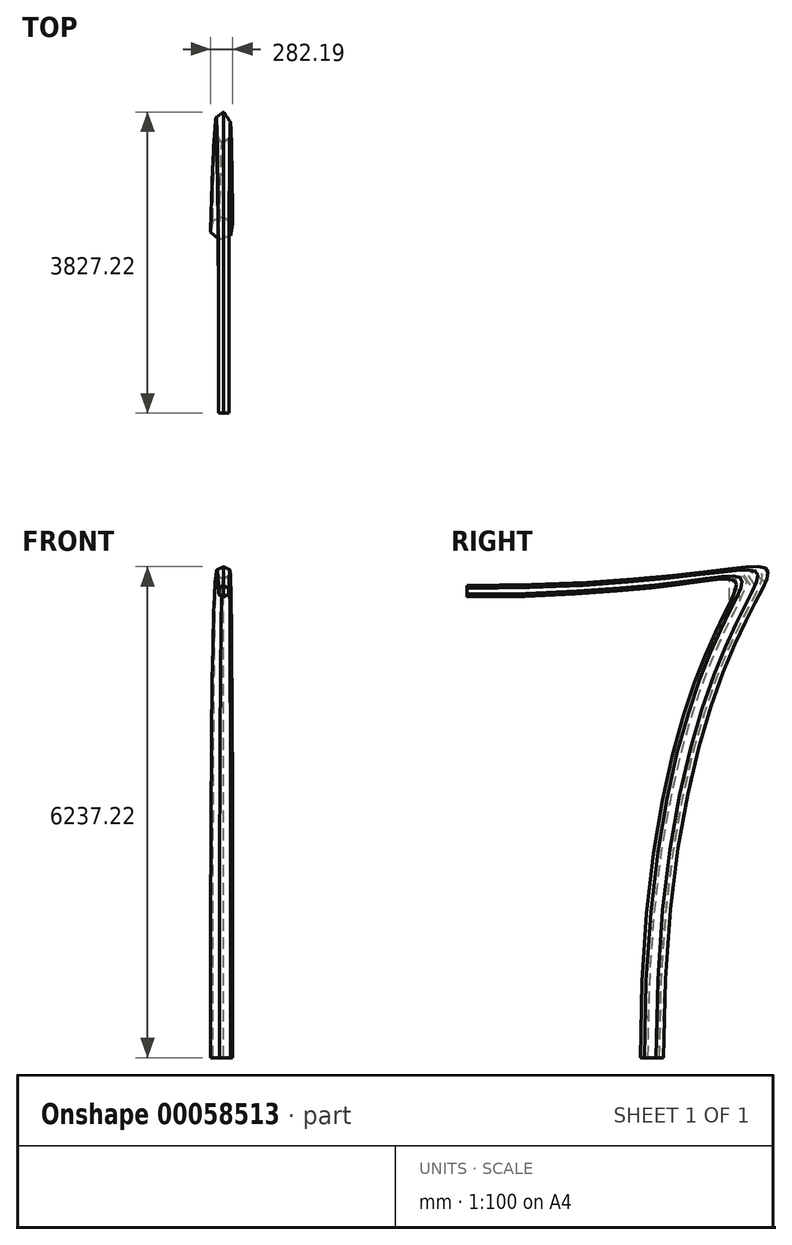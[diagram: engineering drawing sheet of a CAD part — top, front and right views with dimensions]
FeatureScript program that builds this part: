
annotation { "Feature Type Name" : "Feature", "Feature Type Description" : "" }
export const myFeature = defineFeature(function(context is Context, id is Id, definition is map)
    precondition{}
    {
        {
            var Q0;
            Q0=qCreatedBy(makeId("Top.planeOp"),FACE);
            var sketch = newSketch(context, id + "F0", { "sketchPlane" : qUnion([Q0])});
            skCircle(sketch, "E0.cCircle", {"center": v(-26.46, -147.65) * mm, "radius": 150 * mm, "construction": true});
            skLineSegment(sketch, "E0.0", {"start": v(88.18, -244.39) * mm, "end": v(-52.92, -295.3) * mm});
            skLineSegment(sketch, "E0.1", {"start": v(-52.92, -295.3) * mm, "end": v(-167.55, -198.56) * mm});
            skLineSegment(sketch, "E0.2", {"start": v(-167.55, -198.56) * mm, "end": v(-141.1, -50.91) * mm});
            skLineSegment(sketch, "E0.3", {"start": v(-141.1, -50.91) * mm, "end": v(0, 0) * mm});
            skLineSegment(sketch, "E0.4", {"start": v(0, 0) * mm, "end": v(114.64, -96.74) * mm});
            skLineSegment(sketch, "E0.5", {"start": v(114.64, -96.74) * mm, "end": v(88.18, -244.39) * mm});
            skSolve(sketch);
        }
        {
            var Q0;
            Q0=qCreatedBy(makeId("Right.planeOp"),FACE);
            var sketch = newSketch(context, id + "F1", { "sketchPlane" : qUnion([Q0])});
            skLineSegment(sketch, "E1", {"start": v(0, 0) * mm, "end": v(0, 5200) * mm});
            skLineSegment(sketch, "E2", {"start": v(-800, 6000) * mm, "end": v(-2500, 6000) * mm});
            skPoint(sketch, "E3.visualSharp", {"position": v(0, 6000) * mm});
            skArc(sketch, "E3.filletArc", {"start": v(0, 5200) * mm, "mid": v(-234.31, 5765.69) * mm, "end": v(-800, 6000) * mm});
            skSolve(sketch);
        }
        {
            var Q0;
            Q0=sQuery(id+"F1.wireOp",VERTEX,"E2.end");
            var Q1;
            Q1=sQuery(id+"F1.wireOp",EDGE,"E2");
            cPlane(context, id + "F2", {"entities" : qUnion([Q0, Q1]), "cplaneType" : CPlaneType.LINE_POINT, "offset" : 152.4 * mm, "width" : 152.4 * mm, "height" : 152.4 * mm});
        }
        {
            var Q0;
            Q0=qCreatedBy(id+"F2.planeOp",FACE);
            var sketch = newSketch(context, id + "F3", { "sketchPlane" : qUnion([Q0])});
            skCircle(sketch, "E4.cCircle", {"center": v(0, 5925) * mm, "radius": 75 * mm, "construction": true});
            skLineSegment(sketch, "E4.0", {"start": v(0, 5850) * mm, "end": v(-64.95, 5887.5) * mm});
            skLineSegment(sketch, "E4.1", {"start": v(-64.95, 5887.5) * mm, "end": v(-64.95, 5962.5) * mm});
            skLineSegment(sketch, "E4.2", {"start": v(-64.95, 5962.5) * mm, "end": v(0, 6000) * mm});
            skLineSegment(sketch, "E4.3", {"start": v(0, 6000) * mm, "end": v(64.95, 5962.5) * mm});
            skLineSegment(sketch, "E4.4", {"start": v(64.95, 5962.5) * mm, "end": v(64.95, 5887.5) * mm});
            skLineSegment(sketch, "E4.5", {"start": v(64.95, 5887.5) * mm, "end": v(0, 5850) * mm});
            skSolve(sketch);
        }
        {
            var Q0;
            Q0=makeQuery(id+"F0.imprint","IMPRINT",FACE,{"disambiguationData":[TD([[makeQuery(id+"F0.imprint","IMPRINT",EDGE,{"derivedFrom":sQuery(id+"F0.wireOp",EDGE,"E0.0")}),-1.0]])]});
            var Q1;
            Q1=makeQuery(id+"F3.imprint","IMPRINT",FACE,{"disambiguationData":[TD([[makeQuery(id+"F3.imprint","IMPRINT",EDGE,{"derivedFrom":sQuery(id+"F3.wireOp",EDGE,"E4.0")}),-1.0]])]});
            var Q2;
            Q2 = qConstructionFilter(qBodyType(qCreatedBy(id + "F1" ,EDGE), BodyType.WIRE), ConstructionObject.NO);
            var Q3;
            Q3=sQuery(id+"F1.wireOp",VERTEX,"E1.start");
            var Q4;
            Q4=sQuery(id+"F1.wireOp",VERTEX,"E2.end");
            loft(context, id + "F4", {"startCondition" : LoftEndDerivativeType.NORMAL_TO_PROFILE, "startMagnitude" : 4, "endCondition" : LoftEndDerivativeType.NORMAL_TO_PROFILE, "endMagnitude" : 7, "sheetProfilesArray" : [{ "sheetProfileEntities" : qUnion([Q0]) }, { "sheetProfileEntities" : qUnion([Q1]) }], "guidesArray" : [{ "guideEntities" : qUnion([Q2]), "guideDerivativeType" : LoftGuideDerivativeType.DEFAULT, "guideDerivativeMagnitude" : 1 }], "connections" : [{ "connectionEntities" : qUnion([Q3, Q4]), "connectionEdgeQueries" : qUnion([]), "connectionEdgeParameters" : [] }]});
        }
        {
            var Q0;
            Q0=makeQuery(id+"F4.opLoft","CAP_FACE",FACE,{"disambiguationData":[OSD([makeQuery(id+"F3.imprint","IMPRINT",FACE,{"disambiguationData":[TD([[makeQuery(id+"F3.imprint","IMPRINT",EDGE,{"derivedFrom":sQuery(id+"F3.wireOp",EDGE,"E4.0")}),-1.0]])]})])],"isStart":true});
            var Q1;
            Q1=makeQuery(id+"F4.opLoft","CAP_FACE",FACE,{"disambiguationData":[OSD([makeQuery(id+"F0.imprint","IMPRINT",FACE,{"disambiguationData":[TD([[makeQuery(id+"F0.imprint","IMPRINT",EDGE,{"derivedFrom":sQuery(id+"F0.wireOp",EDGE,"E0.0")}),-1.0]])]})])],"isStart":true});
            shell(context, id + "F5", {"entities" : qUnion([Q0, Q1]), "thickness" : 5 * mm});
        }
    });
